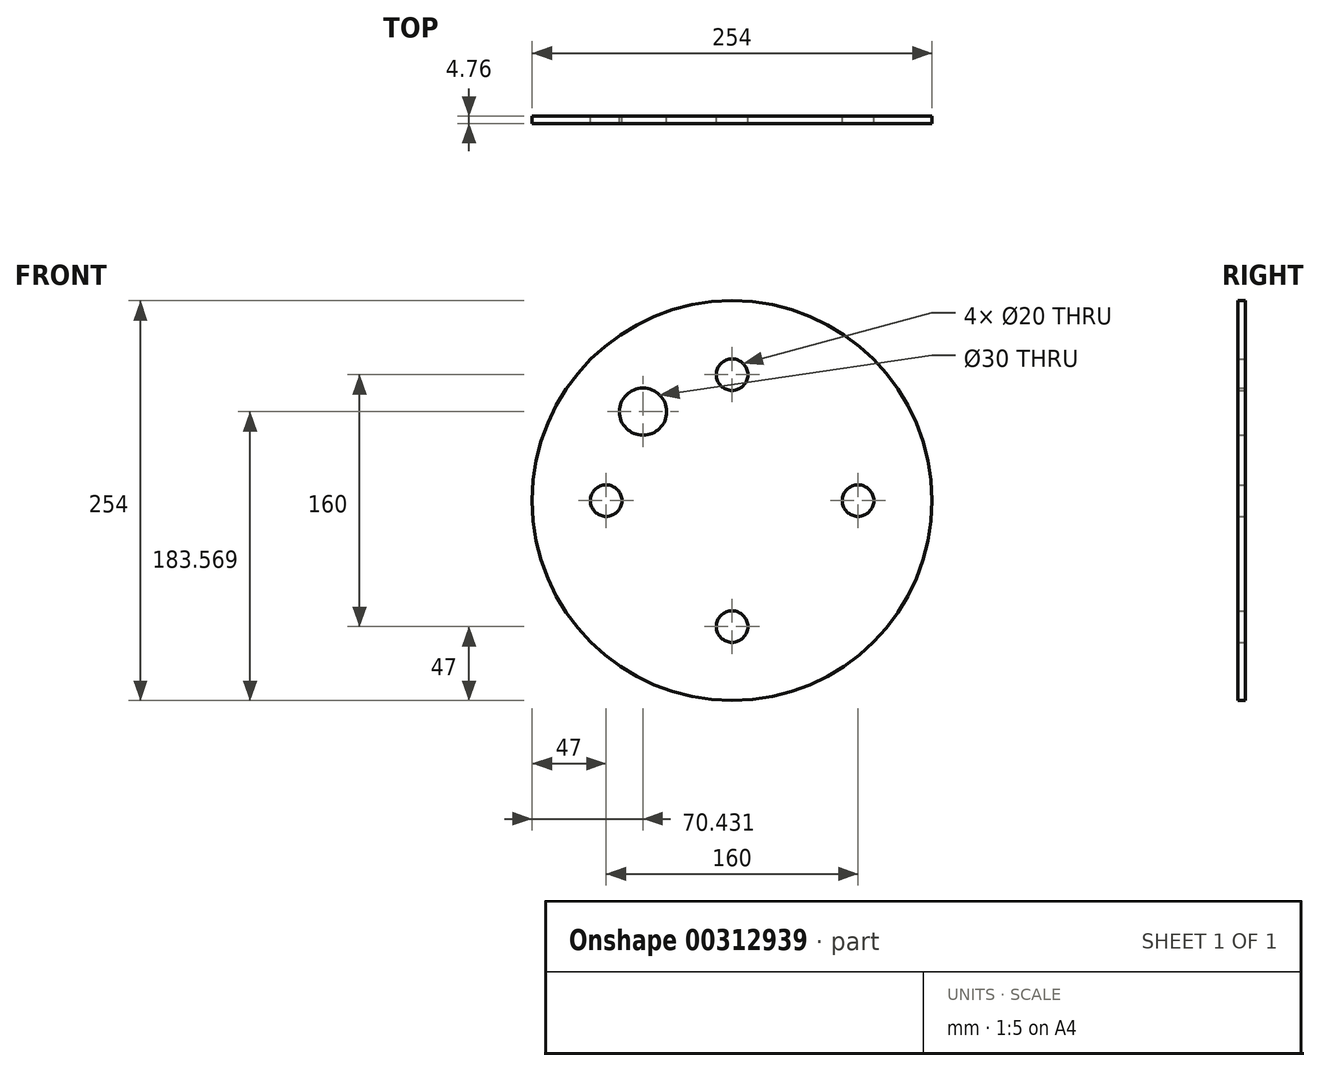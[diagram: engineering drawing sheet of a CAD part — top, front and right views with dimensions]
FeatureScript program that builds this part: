
annotation { "Feature Type Name" : "Feature", "Feature Type Description" : "" }
export const myFeature = defineFeature(function(context is Context, id is Id, definition is map)
    precondition{}
    {
        {
            var Q0;
            Q0=qCreatedBy(makeId("Front.planeOp"),FACE);
            var sketch = newSketch(context, id + "F0", { "sketchPlane" : qUnion([Q0])});
            skCircle(sketch, "E0", {"center": v(0, 0) * mm, "radius": 127 * mm});
            skPoint(sketch, "E1", {"position": v(0, 80) * mm});
            skPoint(sketch, "E2", {"position": v(80, 0) * mm});
            skPoint(sketch, "E3", {"position": v(0, -80) * mm});
            skPoint(sketch, "E4", {"position": v(-80, 0) * mm});
            skCircle(sketch, "E5", {"center": v(0, 80) * mm, "radius": 10 * mm});
            skCircle(sketch, "E6", {"center": v(80, 0) * mm, "radius": 10 * mm});
            skCircle(sketch, "E7", {"center": v(0, -80) * mm, "radius": 10 * mm});
            skCircle(sketch, "E8", {"center": v(-80, 0) * mm, "radius": 10 * mm});
            skPoint(sketch, "E9", {"position": v(-56.57, 56.57) * mm});
            skCircle(sketch, "E10", {"center": v(-56.57, 56.57) * mm, "radius": 15 * mm});
            skSolve(sketch);
        }
        {
            var Q0;
            Q0=makeQuery(id+"F0.imprint","IMPRINT",FACE,{"disambiguationData":[TD([[makeQuery(id+"F0.imprint","IMPRINT",EDGE,{"derivedFrom":sQuery(id+"F0.wireOp",EDGE,"E0")}),1.0]])]});
            extrude(context, id + "F1", {"entities" : qUnion([Q0]), "depth" : 4.76 * mm});
        }
    });
